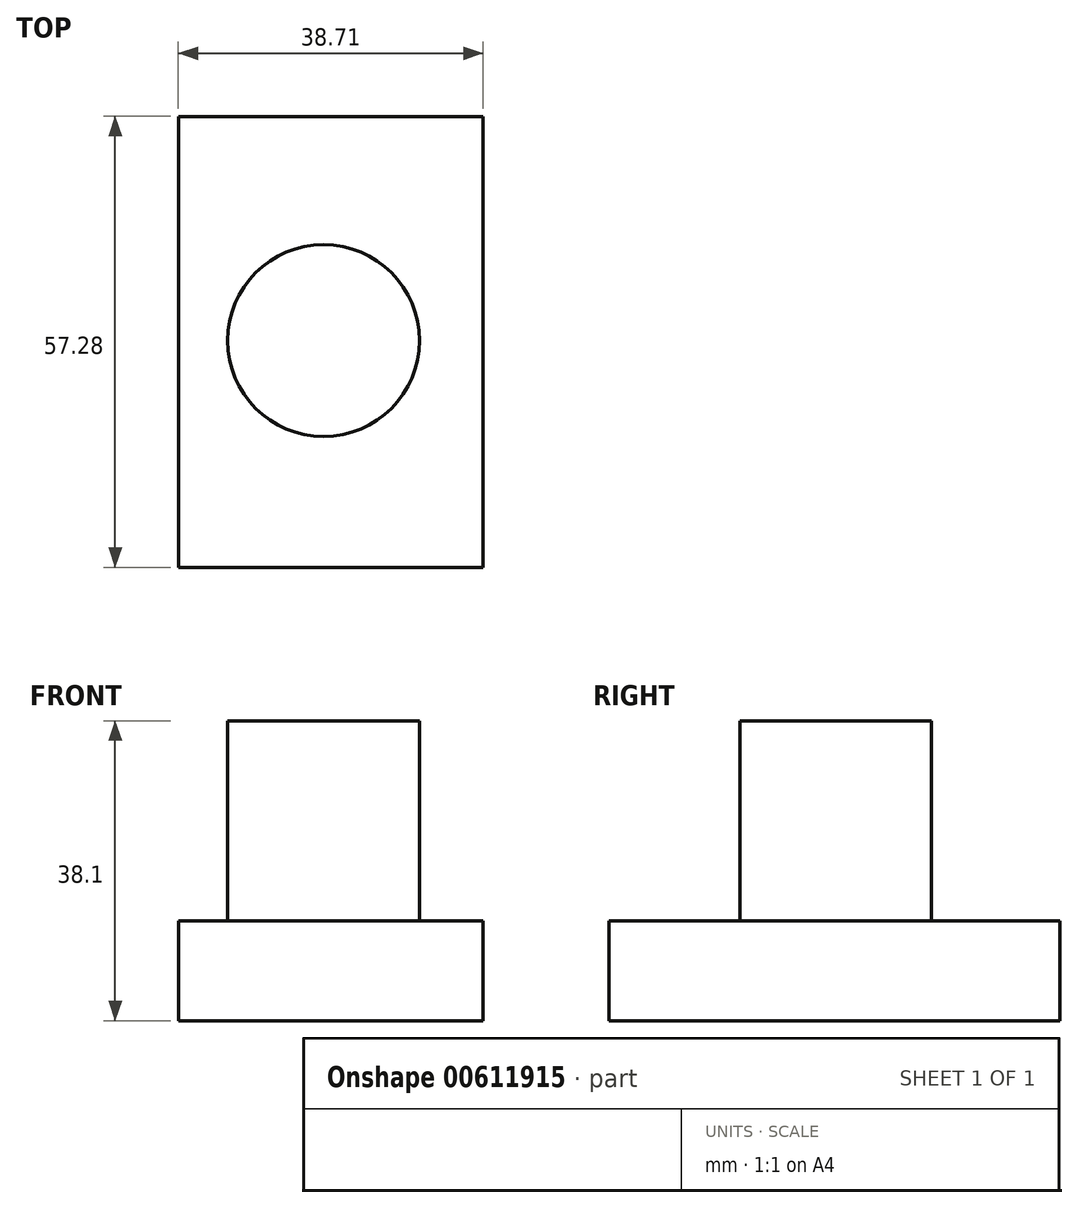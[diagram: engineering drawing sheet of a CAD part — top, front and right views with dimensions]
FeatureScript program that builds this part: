
annotation { "Feature Type Name" : "Feature", "Feature Type Description" : "" }
export const myFeature = defineFeature(function(context is Context, id is Id, definition is map)
    precondition{}
    {
        {
            var Q0;
            Q0=qCreatedBy(makeId("Top.planeOp"),FACE);
            var sketch = newSketch(context, id + "F0", { "sketchPlane" : qUnion([Q0])});
            skLineSegment(sketch, "E0.bottom", {"start": v(-6.33, 0) * mm, "end": v(-45.04, 0) * mm});
            skLineSegment(sketch, "E0.top", {"start": v(-6.33, 57.28) * mm, "end": v(-45.04, 57.28) * mm});
            skLineSegment(sketch, "E0.left", {"start": v(-6.33, 0) * mm, "end": v(-6.33, 57.28) * mm});
            skLineSegment(sketch, "E0.right", {"start": v(-45.04, 0) * mm, "end": v(-45.04, 57.28) * mm});
            skSolve(sketch);
        }
        {
            var Q0;
            Q0=makeQuery(id+"F0.imprint","IMPRINT",FACE,{"disambiguationData":[TD([[makeQuery(id+"F0.imprint","IMPRINT",EDGE,{"derivedFrom":sQuery(id+"F0.wireOp",EDGE,"E0.bottom")}),-1.0]])]});
            extrude(context, id + "F1", {"entities" : qUnion([Q0]), "oppositeDirection" : true, "depth" : 12.7 * mm, "offsetDistance" : 25.4 * mm});
        }
        {
            var Q0;
            Q0=makeQuery(id+"F1.opExtrude","CAP_FACE",FACE,{"disambiguationData":[OSD([sQuery(id+"F0.wireOp",EDGE,"E0.bottom"),sQuery(id+"F0.wireOp",EDGE,"E0.top"),sQuery(id+"F0.wireOp",EDGE,"E0.left"),sQuery(id+"F0.wireOp",EDGE,"E0.right")])],"isStart":true});
            var sketch = newSketch(context, id + "F2", { "sketchPlane" : qUnion([Q0])});
            skCircle(sketch, "E1", {"center": v(-26.6, 28.8) * mm, "radius": 12.17 * mm});
            skSolve(sketch);
        }
        {
            var Q0;
            Q0=makeQuery(id+"F2.imprint","IMPRINT",FACE,{"disambiguationData":[TD([[makeQuery(id+"F2.imprint","IMPRINT",EDGE,{"derivedFrom":sQuery(id+"F2.wireOp",EDGE,"E1")}),1.0]])]});
            extrude(context, id + "F3", {"entities" : qUnion([Q0]), "operationType" : NewBodyOperationType.ADD, "depth" : 25.4 * mm, "offsetDistance" : 25.4 * mm});
        }
    });
